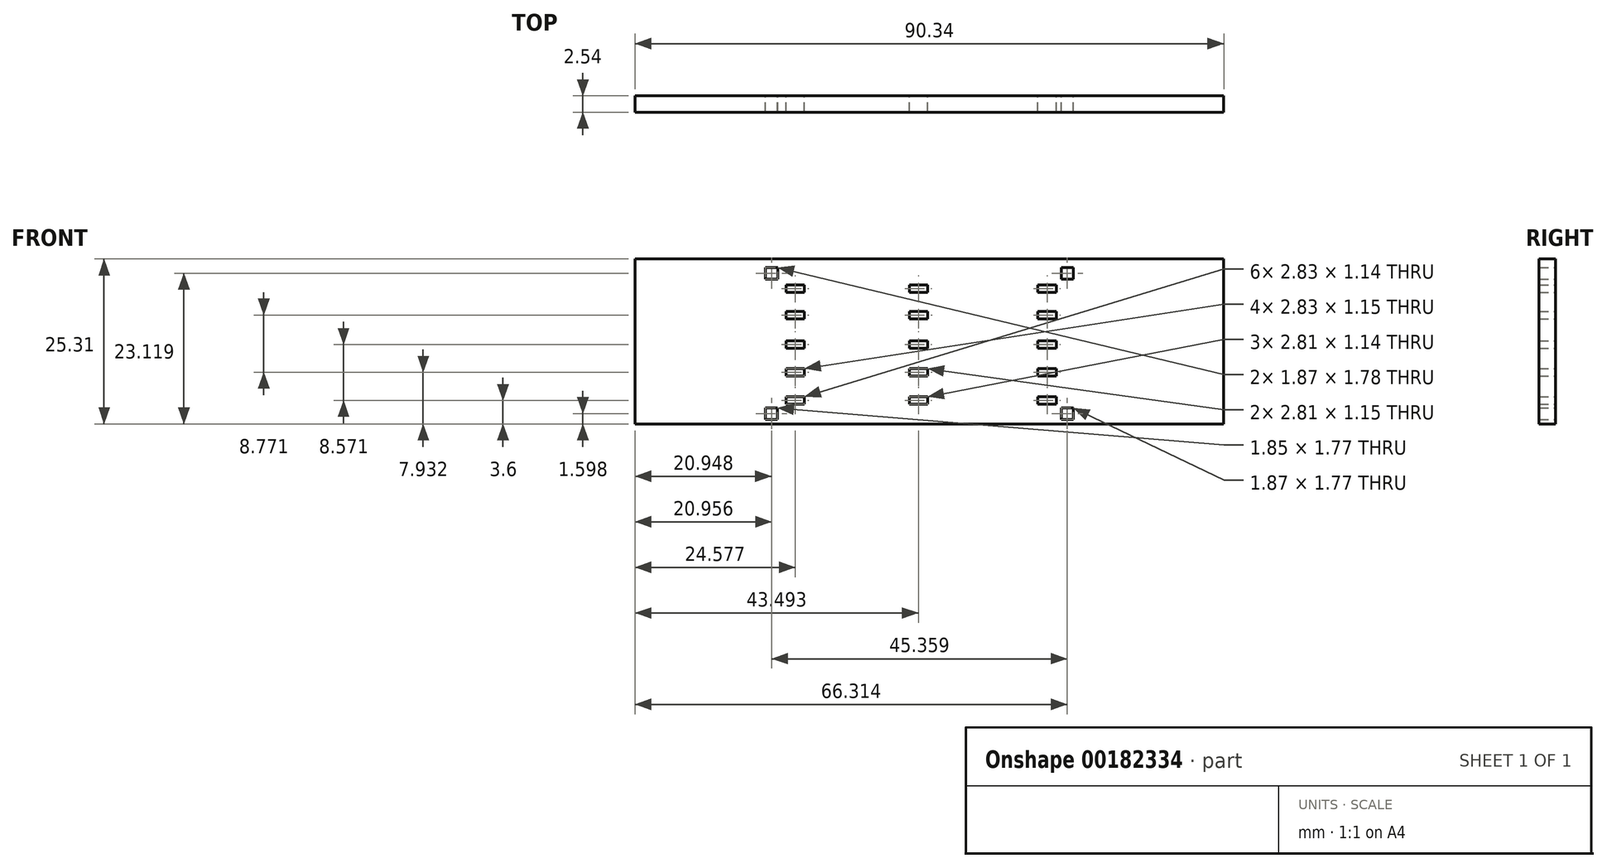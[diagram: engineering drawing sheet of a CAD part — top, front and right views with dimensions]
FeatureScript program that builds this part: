
annotation { "Feature Type Name" : "Feature", "Feature Type Description" : "" }
export const myFeature = defineFeature(function(context is Context, id is Id, definition is map)
    precondition{}
    {
        {
            var Q0;
            Q0=qCreatedBy(makeId("Front.planeOp"),FACE);
            var sketch = newSketch(context, id + "F0", { "sketchPlane" : qUnion([Q0])});
            skLineSegment(sketch, "E0.bottom", {"start": v(-75.23, 61.7) * mm, "end": v(-15.88, 61.7) * mm});
            skLineSegment(sketch, "E0.top", {"start": v(-75.23, 36.4) * mm, "end": v(-15.88, 36.4) * mm});
            skLineSegment(sketch, "E0.left", {"start": v(-75.23, 61.7) * mm, "end": v(-75.23, 36.4) * mm});
            skLineSegment(sketch, "E0.right", {"start": v(-15.88, 61.7) * mm, "end": v(-15.88, 36.4) * mm});
            skLineSegment(sketch, "E1", {"start": v(-69.34, 57.71) * mm, "end": v(-66.5, 57.71) * mm});
            skLineSegment(sketch, "E2", {"start": v(-50.41, 57.71) * mm, "end": v(-47.6, 57.71) * mm});
            skLineSegment(sketch, "E3", {"start": v(-30.68, 57.71) * mm, "end": v(-27.86, 57.71) * mm});
            skLineSegment(sketch, "E4", {"start": v(-69.34, 57.71) * mm, "end": v(-69.34, 56.57) * mm});
            skLineSegment(sketch, "E5", {"start": v(-69.34, 56.57) * mm, "end": v(-66.5, 56.57) * mm});
            skLineSegment(sketch, "E6", {"start": v(-66.5, 56.57) * mm, "end": v(-66.5, 57.71) * mm});
            skLineSegment(sketch, "E7", {"start": v(-50.41, 57.71) * mm, "end": v(-50.41, 56.57) * mm});
            skLineSegment(sketch, "E8", {"start": v(-50.41, 56.57) * mm, "end": v(-47.6, 56.57) * mm});
            skLineSegment(sketch, "E9", {"start": v(-47.6, 56.57) * mm, "end": v(-47.6, 57.71) * mm});
            skLineSegment(sketch, "E10", {"start": v(-30.68, 57.71) * mm, "end": v(-30.68, 56.57) * mm});
            skLineSegment(sketch, "E11", {"start": v(-30.68, 56.57) * mm, "end": v(-27.86, 56.57) * mm});
            skLineSegment(sketch, "E12", {"start": v(-27.86, 56.57) * mm, "end": v(-27.86, 57.71) * mm});
            skLineSegment(sketch, "E13", {"start": v(-69.34, 53.68) * mm, "end": v(-69.34, 52.53) * mm});
            skLineSegment(sketch, "E14", {"start": v(-69.34, 52.53) * mm, "end": v(-66.5, 52.53) * mm});
            skLineSegment(sketch, "E15", {"start": v(-66.5, 52.53) * mm, "end": v(-66.5, 53.68) * mm});
            skLineSegment(sketch, "E16", {"start": v(-66.5, 53.68) * mm, "end": v(-66.5, 52.53) * mm});
            skLineSegment(sketch, "E17", {"start": v(-50.41, 53.68) * mm, "end": v(-50.41, 52.53) * mm});
            skLineSegment(sketch, "E18", {"start": v(-50.41, 52.53) * mm, "end": v(-47.6, 52.53) * mm});
            skLineSegment(sketch, "E19", {"start": v(-47.6, 52.53) * mm, "end": v(-47.6, 53.68) * mm});
            skLineSegment(sketch, "E20", {"start": v(-47.6, 53.68) * mm, "end": v(-47.6, 52.53) * mm});
            skLineSegment(sketch, "E21", {"start": v(-30.68, 53.68) * mm, "end": v(-30.68, 52.53) * mm});
            skLineSegment(sketch, "E22", {"start": v(-30.68, 52.53) * mm, "end": v(-27.86, 52.53) * mm});
            skLineSegment(sketch, "E23", {"start": v(-27.86, 52.53) * mm, "end": v(-27.86, 53.68) * mm});
            skLineSegment(sketch, "E24", {"start": v(-27.86, 53.68) * mm, "end": v(-27.86, 52.53) * mm});
            skLineSegment(sketch, "E25", {"start": v(-69.34, 49.14) * mm, "end": v(-69.34, 48) * mm});
            skLineSegment(sketch, "E26", {"start": v(-69.34, 48) * mm, "end": v(-66.5, 48) * mm});
            skLineSegment(sketch, "E27", {"start": v(-66.5, 48) * mm, "end": v(-66.5, 49.14) * mm});
            skLineSegment(sketch, "E28", {"start": v(-66.5, 49.14) * mm, "end": v(-66.5, 48) * mm});
            skLineSegment(sketch, "E29", {"start": v(-50.41, 49.14) * mm, "end": v(-50.41, 48) * mm});
            skLineSegment(sketch, "E30", {"start": v(-50.41, 48) * mm, "end": v(-47.6, 48) * mm});
            skLineSegment(sketch, "E31", {"start": v(-47.6, 48) * mm, "end": v(-47.6, 49.14) * mm});
            skLineSegment(sketch, "E32", {"start": v(-47.6, 49.14) * mm, "end": v(-47.6, 48) * mm});
            skLineSegment(sketch, "E33", {"start": v(-30.68, 49.14) * mm, "end": v(-30.68, 48) * mm});
            skLineSegment(sketch, "E34", {"start": v(-30.68, 48) * mm, "end": v(-27.86, 48) * mm});
            skLineSegment(sketch, "E35", {"start": v(-27.86, 48) * mm, "end": v(-27.86, 49.14) * mm});
            skLineSegment(sketch, "E36", {"start": v(-27.86, 49.14) * mm, "end": v(-27.86, 48) * mm});
            skLineSegment(sketch, "E37", {"start": v(-69.34, 44.9) * mm, "end": v(-69.34, 43.76) * mm});
            skLineSegment(sketch, "E38", {"start": v(-69.34, 43.76) * mm, "end": v(-66.5, 43.76) * mm});
            skLineSegment(sketch, "E39", {"start": v(-66.5, 43.76) * mm, "end": v(-66.5, 44.9) * mm});
            skLineSegment(sketch, "E40", {"start": v(-66.5, 44.9) * mm, "end": v(-66.5, 43.76) * mm});
            skLineSegment(sketch, "E41", {"start": v(-50.41, 44.9) * mm, "end": v(-50.41, 43.76) * mm});
            skLineSegment(sketch, "E42", {"start": v(-50.41, 43.76) * mm, "end": v(-47.6, 43.76) * mm});
            skLineSegment(sketch, "E43", {"start": v(-47.6, 43.76) * mm, "end": v(-47.6, 44.9) * mm});
            skLineSegment(sketch, "E44", {"start": v(-47.6, 44.9) * mm, "end": v(-47.6, 43.76) * mm});
            skLineSegment(sketch, "E45", {"start": v(-30.68, 44.9) * mm, "end": v(-30.68, 43.76) * mm});
            skLineSegment(sketch, "E46", {"start": v(-30.68, 43.76) * mm, "end": v(-27.86, 43.76) * mm});
            skLineSegment(sketch, "E47", {"start": v(-27.86, 43.76) * mm, "end": v(-27.86, 44.9) * mm});
            skLineSegment(sketch, "E48", {"start": v(-27.86, 44.9) * mm, "end": v(-27.86, 43.76) * mm});
            skLineSegment(sketch, "E49", {"start": v(-69.34, 40.57) * mm, "end": v(-69.34, 39.43) * mm});
            skLineSegment(sketch, "E50", {"start": v(-69.34, 39.43) * mm, "end": v(-66.5, 39.43) * mm});
            skLineSegment(sketch, "E51", {"start": v(-66.5, 39.43) * mm, "end": v(-66.5, 40.57) * mm});
            skLineSegment(sketch, "E52", {"start": v(-66.5, 40.57) * mm, "end": v(-66.5, 39.43) * mm});
            skLineSegment(sketch, "E53", {"start": v(-50.41, 40.57) * mm, "end": v(-50.41, 39.43) * mm});
            skLineSegment(sketch, "E54", {"start": v(-50.41, 39.43) * mm, "end": v(-47.6, 39.43) * mm});
            skLineSegment(sketch, "E55", {"start": v(-47.6, 39.43) * mm, "end": v(-47.6, 40.57) * mm});
            skLineSegment(sketch, "E56", {"start": v(-47.6, 40.57) * mm, "end": v(-47.6, 39.43) * mm});
            skLineSegment(sketch, "E57", {"start": v(-30.68, 40.57) * mm, "end": v(-30.68, 39.43) * mm});
            skLineSegment(sketch, "E58", {"start": v(-30.68, 39.43) * mm, "end": v(-27.86, 39.43) * mm});
            skLineSegment(sketch, "E59", {"start": v(-27.86, 39.43) * mm, "end": v(-27.86, 40.57) * mm});
            skLineSegment(sketch, "E60", {"start": v(-27.86, 40.57) * mm, "end": v(-27.86, 39.43) * mm});
            skLineSegment(sketch, "E61", {"start": v(-69.34, 53.68) * mm, "end": v(-66.5, 53.68) * mm});
            skLineSegment(sketch, "E62", {"start": v(-50.41, 53.68) * mm, "end": v(-47.6, 53.68) * mm});
            skLineSegment(sketch, "E63", {"start": v(-30.68, 53.68) * mm, "end": v(-27.86, 53.68) * mm});
            skLineSegment(sketch, "E64", {"start": v(-30.68, 49.14) * mm, "end": v(-27.86, 49.14) * mm});
            skLineSegment(sketch, "E65", {"start": v(-50.41, 49.14) * mm, "end": v(-47.6, 49.14) * mm});
            skLineSegment(sketch, "E66", {"start": v(-69.34, 49.14) * mm, "end": v(-66.5, 49.14) * mm});
            skLineSegment(sketch, "E67", {"start": v(-69.34, 44.9) * mm, "end": v(-66.5, 44.9) * mm});
            skLineSegment(sketch, "E68", {"start": v(-50.41, 44.9) * mm, "end": v(-47.6, 44.9) * mm});
            skLineSegment(sketch, "E69", {"start": v(-30.68, 44.9) * mm, "end": v(-27.86, 44.9) * mm});
            skLineSegment(sketch, "E70", {"start": v(-30.68, 40.57) * mm, "end": v(-27.86, 40.57) * mm});
            skLineSegment(sketch, "E71", {"start": v(-50.41, 40.57) * mm, "end": v(-47.6, 40.57) * mm});
            skLineSegment(sketch, "E72", {"start": v(-69.34, 40.57) * mm, "end": v(-66.5, 40.57) * mm});
            skSolve(sketch);
        }
        {
            var Q0;
            Q0=qCreatedBy(makeId("Front.planeOp"),FACE);
            var sketch = newSketch(context, id + "F1", { "sketchPlane" : qUnion([Q0])});
            skLineSegment(sketch, "E73.bottom", {"start": v(-72.48, 60.4) * mm, "end": v(-70.61, 60.4) * mm});
            skLineSegment(sketch, "E73.top", {"start": v(-72.48, 58.63) * mm, "end": v(-70.61, 58.63) * mm});
            skLineSegment(sketch, "E73.left", {"start": v(-72.48, 60.4) * mm, "end": v(-72.48, 58.63) * mm});
            skLineSegment(sketch, "E73.right", {"start": v(-70.61, 60.4) * mm, "end": v(-70.61, 58.63) * mm});
            skPoint(sketch, "E74.firstSnap0", {"position": v(-70.61, 59.52) * mm});
            skLineSegment(sketch, "E75.bottom", {"start": v(-27.12, 60.4) * mm, "end": v(-25.25, 60.4) * mm});
            skLineSegment(sketch, "E75.top", {"start": v(-27.12, 58.63) * mm, "end": v(-25.25, 58.63) * mm});
            skLineSegment(sketch, "E75.left", {"start": v(-27.12, 60.4) * mm, "end": v(-27.12, 58.63) * mm});
            skLineSegment(sketch, "E75.right", {"start": v(-25.25, 60.4) * mm, "end": v(-25.25, 58.63) * mm});
            skLineSegment(sketch, "E76.bottom", {"start": v(-72.48, 38.88) * mm, "end": v(-70.63, 38.88) * mm});
            skLineSegment(sketch, "E76.top", {"start": v(-72.48, 37.11) * mm, "end": v(-70.63, 37.11) * mm});
            skLineSegment(sketch, "E76.left", {"start": v(-72.48, 38.88) * mm, "end": v(-72.48, 37.11) * mm});
            skLineSegment(sketch, "E76.right", {"start": v(-70.63, 38.88) * mm, "end": v(-70.63, 37.11) * mm});
            skLineSegment(sketch, "E77.bottom", {"start": v(-27.12, 37.11) * mm, "end": v(-25.25, 37.11) * mm});
            skLineSegment(sketch, "E77.top", {"start": v(-27.12, 38.88) * mm, "end": v(-25.25, 38.88) * mm});
            skLineSegment(sketch, "E77.left", {"start": v(-27.12, 37.11) * mm, "end": v(-27.12, 38.88) * mm});
            skLineSegment(sketch, "E77.right", {"start": v(-25.25, 37.11) * mm, "end": v(-25.25, 38.88) * mm});
            skSolve(sketch);
        }
        {
            var Q0;
            Q0 = qSketchRegion(id + "F0", true);
            extrude(context, id + "F2", {"entities" : qUnion([Q0]), "depth" : 2.54 * mm});
        }
        {
            var Q0;
            Q0 = qSketchRegion(id + "F1", true);
            extrude(context, id + "F3", {"entities" : qUnion([Q0]), "operationType" : NewBodyOperationType.REMOVE, "depth" : 25.4 * mm});
        }
        {
            var Q0;
            Q0=makeQuery(id+"F2.opExtrude","SWEPT_FACE",FACE,{"disambiguationData":[OSD([sQuery(id+"F0.wireOp",EDGE,"E0.right")])]});
            extrude(context, id + "F4", {"entities" : qUnion([Q0]), "operationType" : NewBodyOperationType.ADD, "depth" : 13.72 * mm});
        }
        {
            var Q0;
            Q0=makeQuery(id+"F2.opExtrude","SWEPT_FACE",FACE,{"disambiguationData":[OSD([sQuery(id+"F0.wireOp",EDGE,"E0.left")])]});
            extrude(context, id + "F5", {"entities" : qUnion([Q0]), "operationType" : NewBodyOperationType.ADD, "depth" : 17.27 * mm});
        }
    });
